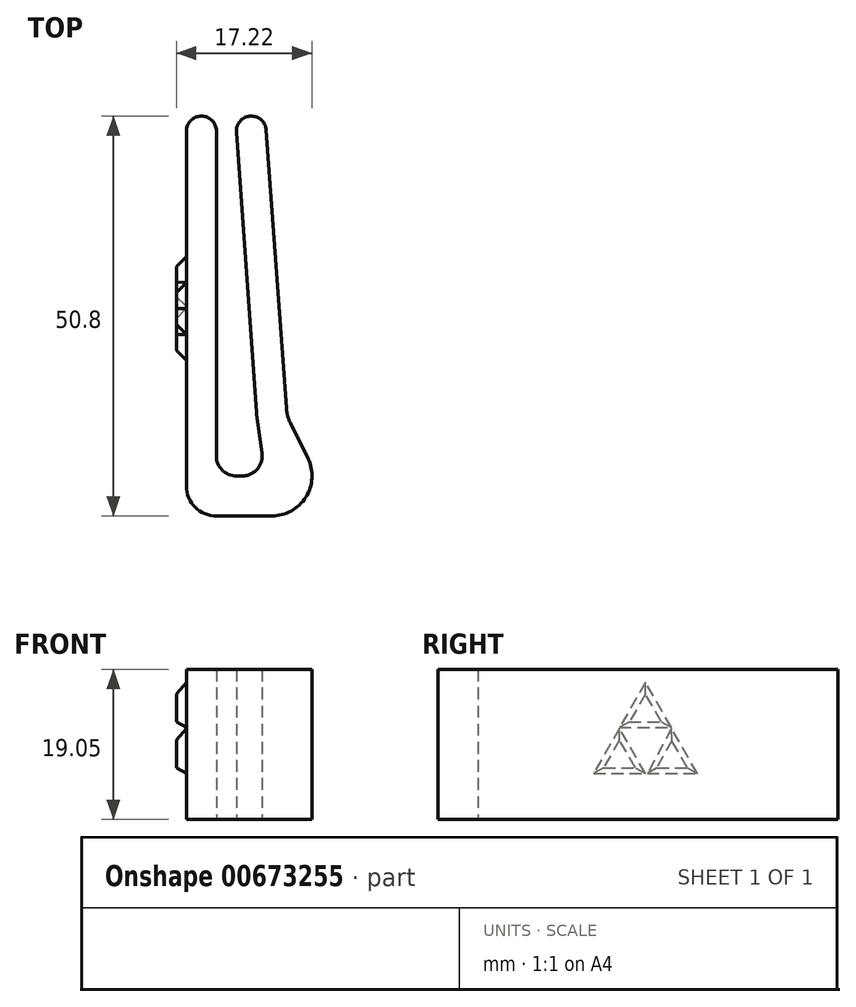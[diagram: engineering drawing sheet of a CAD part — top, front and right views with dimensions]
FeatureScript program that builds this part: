
annotation { "Feature Type Name" : "Feature", "Feature Type Description" : "" }
export const myFeature = defineFeature(function(context is Context, id is Id, definition is map)
    precondition{}
    {
        {
            var Q0;
            Q0=qCreatedBy(makeId("Top.planeOp"),FACE);
            var sketch = newSketch(context, id + "F0", { "sketchPlane" : qUnion([Q0])});
            skLineSegment(sketch, "E0", {"start": v(0, 3.8) * mm, "end": v(0, 48.9) * mm});
            skLineSegment(sketch, "E1", {"start": v(1.9, 50.8) * mm, "end": v(1.9, 50.8) * mm});
            skLineSegment(sketch, "E2", {"start": v(3.81, 48.9) * mm, "end": v(3.81, 7.62) * mm});
            skLineSegment(sketch, "E3", {"start": v(6.35, 5.08) * mm, "end": v(7.1, 5.08) * mm});
            skLineSegment(sketch, "E4", {"start": v(9.6, 7.97) * mm, "end": v(8.92, 12.87) * mm});
            skLineSegment(sketch, "E5", {"start": v(8.9, 13.13) * mm, "end": v(6.35, 48.76) * mm});
            skLineSegment(sketch, "E6", {"start": v(8.24, 50.8) * mm, "end": v(8.25, 50.8) * mm});
            skLineSegment(sketch, "E7", {"start": v(10.14, 49.03) * mm, "end": v(12.7, 13.68) * mm});
            skLineSegment(sketch, "E8", {"start": v(13.21, 11.8) * mm, "end": v(15.42, 7.33) * mm});
            skLineSegment(sketch, "E9", {"start": v(10.87, 0) * mm, "end": v(3.81, 0) * mm});
            skPoint(sketch, "E10.visualSharp", {"position": v(0, 50.8) * mm});
            skArc(sketch, "E10.filletArc", {"start": v(1.9, 50.8) * mm, "mid": v(0.56, 50.24) * mm, "end": v(0, 48.9) * mm});
            skPoint(sketch, "E11.visualSharp", {"position": v(3.8, 50.8) * mm});
            skArc(sketch, "E11.filletArc", {"start": v(3.8, 48.9) * mm, "mid": v(3.25, 50.24) * mm, "end": v(1.9, 50.8) * mm});
            skPoint(sketch, "E12.visualSharp", {"position": v(6.2, 50.8) * mm});
            skArc(sketch, "E12.filletArc", {"start": v(8.25, 50.8) * mm, "mid": v(6.86, 50.2) * mm, "end": v(6.35, 48.76) * mm});
            skPoint(sketch, "E13.visualSharp", {"position": v(10.01, 50.8) * mm});
            skArc(sketch, "E13.filletArc", {"start": v(10.14, 49.03) * mm, "mid": v(9.54, 50.29) * mm, "end": v(8.24, 50.8) * mm});
            skPoint(sketch, "E14.visualSharp", {"position": v(3.81, 5.08) * mm});
            skArc(sketch, "E14.filletArc", {"start": v(3.81, 7.62) * mm, "mid": v(4.55, 5.82) * mm, "end": v(6.35, 5.08) * mm});
            skPoint(sketch, "E15.visualSharp", {"position": v(8.9, 13) * mm});
            skArc(sketch, "E15.filletArc", {"start": v(8.89, 13.13) * mm, "mid": v(8.9, 13) * mm, "end": v(8.92, 12.87) * mm});
            skPoint(sketch, "E16.visualSharp", {"position": v(10.01, 5.08) * mm});
            skArc(sketch, "E16.filletArc", {"start": v(7.1, 5.08) * mm, "mid": v(9, 5.95) * mm, "end": v(9.6, 7.97) * mm});
            skPoint(sketch, "E17.visualSharp", {"position": v(19.05, 0) * mm});
            skArc(sketch, "E17.filletArc", {"start": v(10.87, 0) * mm, "mid": v(15.19, 2.4) * mm, "end": v(15.42, 7.33) * mm});
            skPoint(sketch, "E18.visualSharp", {"position": v(0, 0) * mm});
            skArc(sketch, "E18.filletArc", {"start": v(0, 3.8) * mm, "mid": v(1.12, 1.12) * mm, "end": v(3.81, 0) * mm});
            skPoint(sketch, "E19.visualSharp", {"position": v(12.77, 12.7) * mm});
            skArc(sketch, "E19.filletArc", {"start": v(12.7, 13.68) * mm, "mid": v(12.87, 12.72) * mm, "end": v(13.21, 11.8) * mm});
            skSolve(sketch);
        }
        {
            var Q0;
            Q0=makeQuery(id+"F0.imprint","IMPRINT",FACE,{"disambiguationData":[TD([[makeQuery(id+"F0.imprint","IMPRINT",EDGE,{"derivedFrom":sQuery(id+"F0.wireOp",EDGE,"E0")}),-1.0]])]});
            extrude(context, id + "F1", {"entities" : qUnion([Q0]), "depth" : 19.05 * mm, "offsetDistance" : 25.4 * mm});
        }
        {
            var Q0;
            Q0=makeQuery(id+"F1.opExtrude","SWEPT_FACE",FACE,{"disambiguationData":[OSD([sQuery(id+"F0.wireOp",EDGE,"E0")])]});
            var sketch = newSketch(context, id + "F2", { "sketchPlane" : qUnion([Q0])});
            skLineSegment(sketch, "E20.0", {"start": v(-23.05, 11.68) * mm, "end": v(-29.65, 11.68) * mm});
            skLineSegment(sketch, "E20.1", {"start": v(-29.65, 11.68) * mm, "end": v(-26.35, 17.4) * mm});
            skLineSegment(sketch, "E20.2", {"start": v(-26.35, 17.4) * mm, "end": v(-23.05, 11.68) * mm});
            skPoint(sketch, "E20.0.midPoint", {"position": v(-26.35, 11.68) * mm});
            skLineSegment(sketch, "E21.0", {"start": v(-26.6, 5.84) * mm, "end": v(-32.98, 5.84) * mm});
            skLineSegment(sketch, "E21.1", {"start": v(-32.98, 5.84) * mm, "end": v(-29.68, 11.56) * mm});
            skLineSegment(sketch, "E21.2", {"start": v(-29.68, 11.56) * mm, "end": v(-26.6, 5.84) * mm});
            skLineSegment(sketch, "E22.0", {"start": v(-19.75, 5.84) * mm, "end": v(-26.35, 5.84) * mm});
            skLineSegment(sketch, "E22.1", {"start": v(-26.35, 5.84) * mm, "end": v(-23.05, 11.56) * mm});
            skLineSegment(sketch, "E22.2", {"start": v(-23.05, 11.56) * mm, "end": v(-19.75, 5.84) * mm});
            skSolve(sketch);
        }
        {
            var Q0;
            Q0 = qSketchRegion(id + "F2", true);
            extrude(context, id + "F3", {"entities" : qUnion([Q0]), "depth" : 1.27 * mm, "offsetDistance" : 25.4 * mm, "hasDraft" : true, "draftAngle" : 30 * degree, "draftPullDirection" : true});
        }
    });
